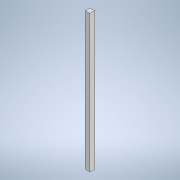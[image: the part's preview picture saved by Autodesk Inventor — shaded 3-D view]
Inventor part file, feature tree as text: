
AUTODESK INVENTOR PART (.ipt)
format: ipt  version: 2021 (Build 250183000, 183)  size: 94,720 bytes
history: native  units: mm
features: extrude x1, sketch x1
ambient origin geometry x8: Origin, YZ Plane, XZ Plane, XY Plane, X Axis, Y Axis, Z Axis, Center Point
bodies: Solid1 (feature_tree)
feature tree (2):
  extrude  "Extrusion1"  Depth=13.0mm
  sketch  "Sketch1"  dims[d0=13.0mm d1=13.0mm d2=379.0mm d3=0.0mm d4=0.5mm d5=0.872665mm d6=0.5mm d7=0.872665mm]
